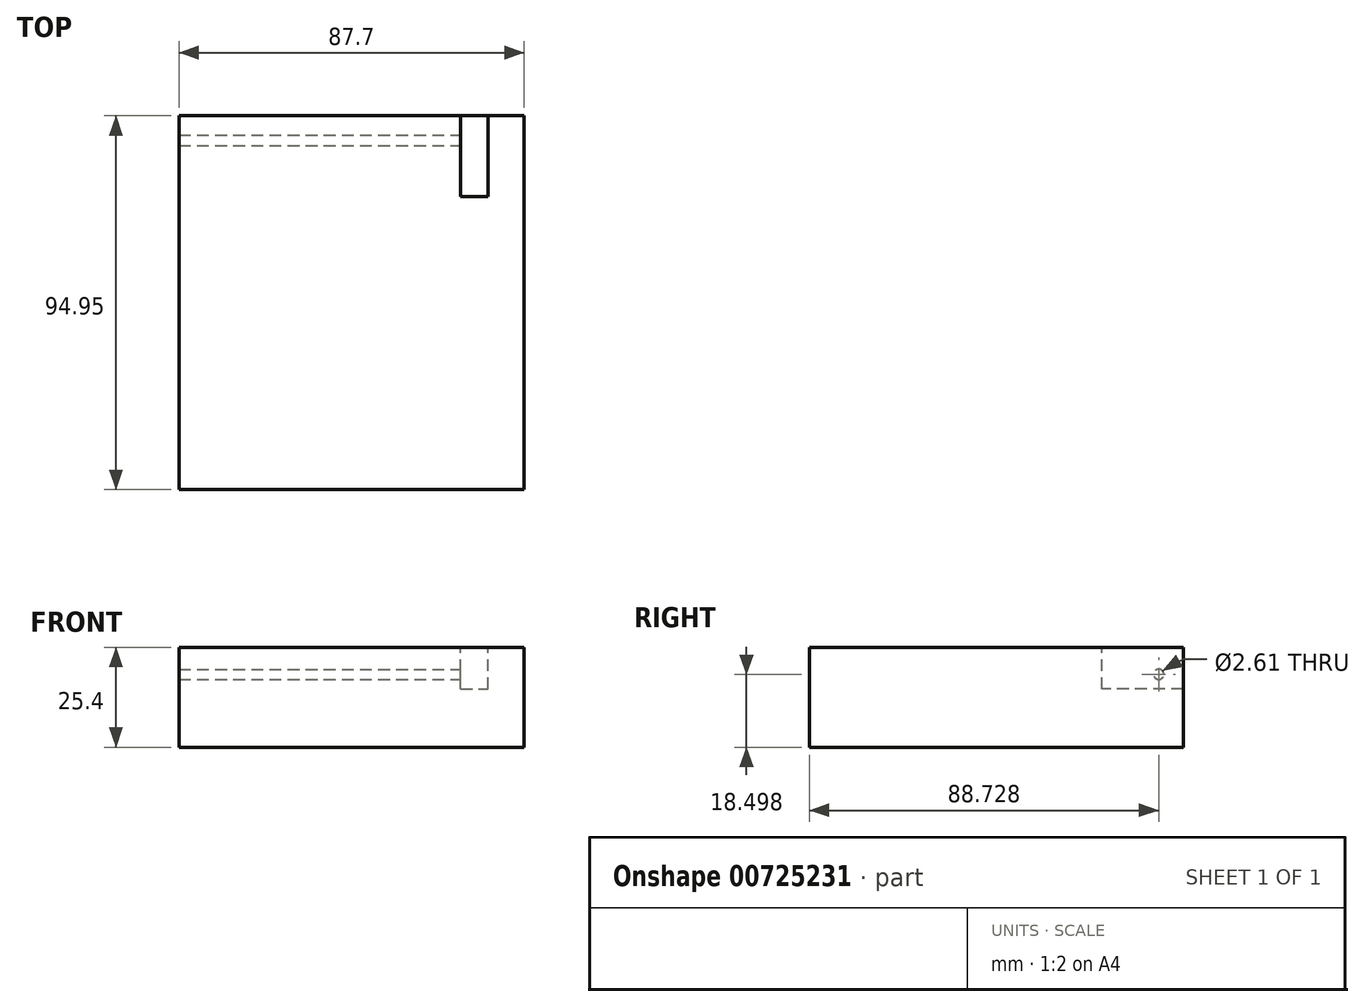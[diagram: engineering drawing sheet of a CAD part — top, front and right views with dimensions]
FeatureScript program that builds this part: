
annotation { "Feature Type Name" : "Feature", "Feature Type Description" : "" }
export const myFeature = defineFeature(function(context is Context, id is Id, definition is map)
    precondition{}
    {
        {
            var Q0;
            Q0=qCreatedBy(makeId("Top.planeOp"),FACE);
            var sketch = newSketch(context, id + "F0", { "sketchPlane" : qUnion([Q0])});
            skLineSegment(sketch, "E0.bottom", {"start": v(-36.71, 30.58) * mm, "end": v(51, 30.58) * mm});
            skLineSegment(sketch, "E0.top", {"start": v(-36.71, -64.37) * mm, "end": v(51, -64.37) * mm});
            skLineSegment(sketch, "E0.left", {"start": v(-36.71, 30.58) * mm, "end": v(-36.71, -64.37) * mm});
            skLineSegment(sketch, "E0.right", {"start": v(51, 30.58) * mm, "end": v(51, -64.37) * mm});
            skSolve(sketch);
        }
        {
            var Q0;
            Q0=makeQuery(id+"F0.imprint","IMPRINT",FACE,{"disambiguationData":[TD([[makeQuery(id+"F0.imprint","IMPRINT",EDGE,{"derivedFrom":sQuery(id+"F0.wireOp",EDGE,"E0.bottom")}),-1.0]])]});
            extrude(context, id + "F1", {"entities" : qUnion([Q0]), "depth" : 25.4 * mm, "offsetDistance" : 25.4 * mm});
        }
        {
            var Q0;
            Q0=makeQuery(id+"F1.opExtrude","CAP_FACE",FACE,{"disambiguationData":[OSD([sQuery(id+"F0.wireOp",EDGE,"E0.bottom"),sQuery(id+"F0.wireOp",EDGE,"E0.top"),sQuery(id+"F0.wireOp",EDGE,"E0.left"),sQuery(id+"F0.wireOp",EDGE,"E0.right")])],"isStart":false});
            var sketch = newSketch(context, id + "F2", { "sketchPlane" : qUnion([Q0])});
            skCircle(sketch, "E1", {"center": v(-22.23, 13.5) * mm, "radius": 10.77 * mm});
            skCircle(sketch, "E2", {"center": v(31.09, 14.71) * mm, "radius": 11.22 * mm});
            skCircle(sketch, "E3", {"center": v(-16.32, -29.93) * mm, "radius": 8.09 * mm});
            skCircle(sketch, "E4", {"center": v(29.76, -11.83) * mm, "radius": 6.03 * mm});
            skSolve(sketch);
        }
        {
            var Q0;
            Q0 = qSketchRegion(id + "F2", true);
            var Q1;
            Q1=makeQuery(id+"F2.imprint","IMPRINT",FACE,{"disambiguationData":[TD([[makeQuery(id+"F2.imprint","IMPRINT",EDGE,{"derivedFrom":sQuery(id+"F2.wireOp",EDGE,"E1")}),1.0]])]});
            var Q2;
            Q2=sQuery(id+"F2.wireOp",EDGE,"E1");
            extrude(context, id + "F3", {"entities" : qUnion([Q0, Q1]), "bodyType" : ToolBodyType.SURFACE, "surfaceEntities" : qUnion([Q2]), "depth" : 25.4 * mm, "offsetDistance" : 25.4 * mm});
        }
        {
            var Q0;
            Q0=makeQuery(id+"F1.opExtrude","CAP_FACE",FACE,{"disambiguationData":[OSD([sQuery(id+"F0.wireOp",EDGE,"E0.bottom"),sQuery(id+"F0.wireOp",EDGE,"E0.top"),sQuery(id+"F0.wireOp",EDGE,"E0.left"),sQuery(id+"F0.wireOp",EDGE,"E0.right")])],"isStart":false});
            var sketch = newSketch(context, id + "F4", { "sketchPlane" : qUnion([Q0])});
            skLineSegment(sketch, "E5.bottom", {"start": v(41.76, 30.58) * mm, "end": v(34.87, 30.58) * mm});
            skLineSegment(sketch, "E5.top", {"start": v(41.76, 9.98) * mm, "end": v(34.87, 9.98) * mm});
            skLineSegment(sketch, "E5.left", {"start": v(41.76, 30.58) * mm, "end": v(41.76, 9.98) * mm});
            skLineSegment(sketch, "E5.right", {"start": v(34.87, 30.58) * mm, "end": v(34.87, 9.98) * mm});
            skSolve(sketch);
        }
        {
            var Q0;
            Q0 = qSketchRegion(id + "F4", true);
            extrude(context, id + "F5", {"entities" : qUnion([Q0]), "operationType" : NewBodyOperationType.REMOVE, "oppositeDirection" : true, "depth" : 10.64 * mm, "offsetDistance" : 25.4 * mm});
        }
        {
            var Q0;
            Q0=makeQuery(id+"F5.boolean.opBoolean","COPY",FACE,{"derivedFrom":makeQuery(id+"F5.opExtrude","SWEPT_FACE",FACE,{"disambiguationData":[OSD([sQuery(id+"F4.wireOp",EDGE,"E5.right")])]})});
            var sketch = newSketch(context, id + "F6", { "sketchPlane" : qUnion([Q0])});
            skCircle(sketch, "E6", {"center": v(24.36, 18.5) * mm, "radius": 1.3 * mm});
            skSolve(sketch);
        }
        {
            var Q0;
            Q0 = qSketchRegion(id + "F6", true);
            extrude(context, id + "F7", {"entities" : qUnion([Q0]), "operationType" : NewBodyOperationType.REMOVE, "endBound" : BoundingType.THROUGH_ALL, "oppositeDirection" : true, "depth" : 25.4 * mm, "offsetDistance" : 25.4 * mm});
        }
    });
